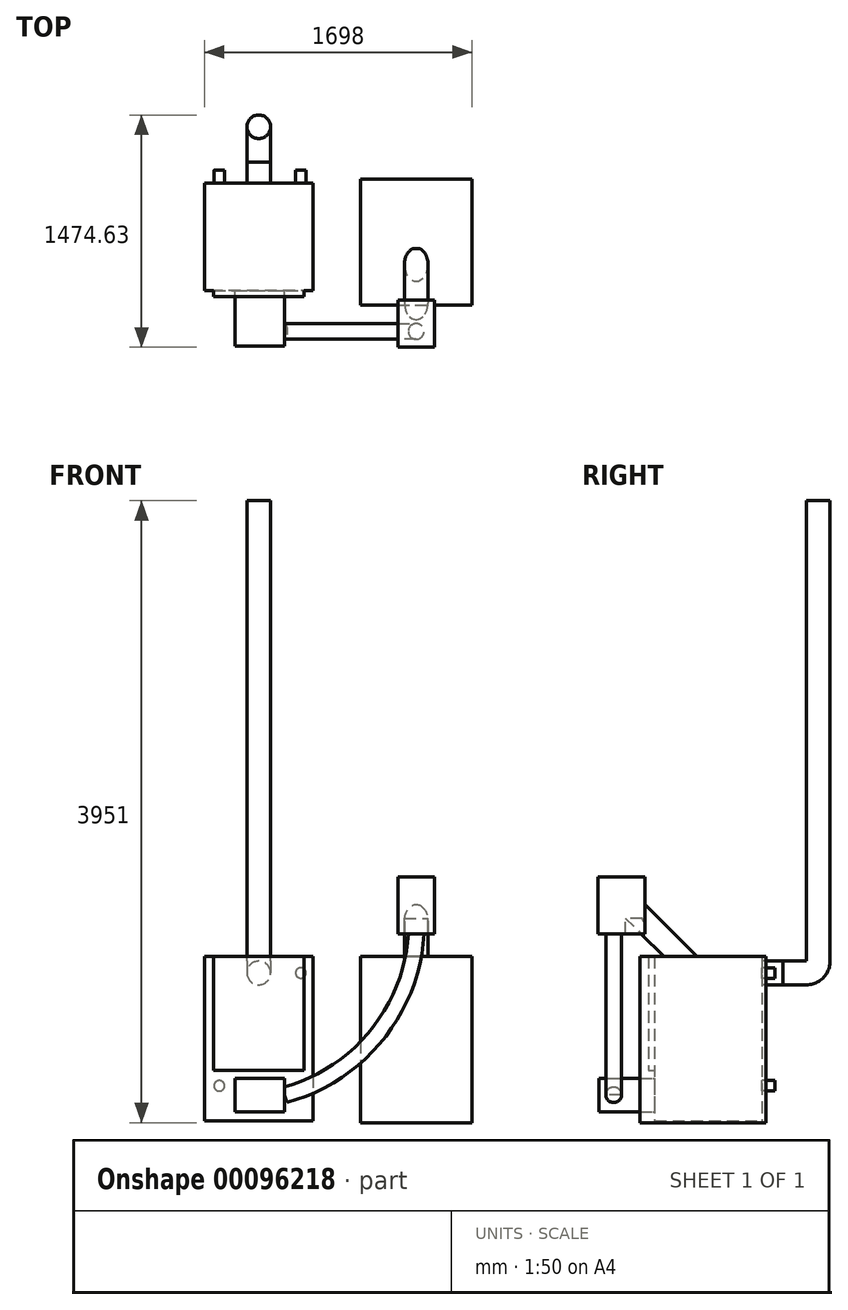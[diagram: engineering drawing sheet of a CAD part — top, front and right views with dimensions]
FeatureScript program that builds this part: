
annotation { "Feature Type Name" : "Feature", "Feature Type Description" : "" }
export const myFeature = defineFeature(function(context is Context, id is Id, definition is map)
    precondition{}
    {
        {
            var Q0;
            Q0=qCreatedBy(makeId("Front.planeOp"),FACE);
            var sketch = newSketch(context, id + "F0", { "sketchPlane" : qUnion([Q0])});
            skLineSegment(sketch, "E0.bottom", {"start": v(344, 522.5) * mm, "end": v(-344, 522.5) * mm});
            skLineSegment(sketch, "E0.top", {"start": v(344, -522.5) * mm, "end": v(-344, -522.5) * mm});
            skLineSegment(sketch, "E0.left", {"start": v(344, 522.5) * mm, "end": v(344, -522.5) * mm});
            skLineSegment(sketch, "E0.right", {"start": v(-344, 522.5) * mm, "end": v(-344, -522.5) * mm});
            skPoint(sketch, "E0.middle", {"position": v(0, 0) * mm});
            skSolve(sketch);
        }
        {
            var Q0;
            Q0 = qSketchRegion(id + "F0", true);
            extrude(context, id + "F1", {"entities" : qUnion([Q0]), "endBound" : BoundingType.SYMMETRIC, "depth" : 682 * mm});
        }
        {
            var Q0;
            Q0=makeQuery(id+"F1.opExtrude","CAP_FACE",FACE,{"disambiguationData":[OSD([sQuery(id+"F0.wireOp",EDGE,"E0.bottom"),sQuery(id+"F0.wireOp",EDGE,"E0.top"),sQuery(id+"F0.wireOp",EDGE,"E0.left"),sQuery(id+"F0.wireOp",EDGE,"E0.right")])],"isStart":false});
            var sketch = newSketch(context, id + "F2", { "sketchPlane" : qUnion([Q0])});
            skLineSegment(sketch, "E1.bottom", {"start": v(-287, 522.5) * mm, "end": v(287, 522.5) * mm});
            skLineSegment(sketch, "E1.top", {"start": v(-287, -200.5) * mm, "end": v(287, -200.5) * mm});
            skLineSegment(sketch, "E1.left", {"start": v(-287, 522.5) * mm, "end": v(-287, -200.5) * mm});
            skLineSegment(sketch, "E1.right", {"start": v(287, 522.5) * mm, "end": v(287, -200.5) * mm});
            skPoint(sketch, "E2", {"position": v(0, 522.5) * mm});
            skSolve(sketch);
        }
        {
            var Q0;
            Q0 = qSketchRegion(id + "F2", true);
            extrude(context, id + "F3", {"entities" : qUnion([Q0]), "operationType" : NewBodyOperationType.ADD, "depth" : 38.7 * mm});
        }
        {
            var Q0;
            Q0=makeQuery(id+"F1.opExtrude","CAP_FACE",FACE,{"disambiguationData":[OSD([sQuery(id+"F0.wireOp",EDGE,"E0.bottom"),sQuery(id+"F0.wireOp",EDGE,"E0.top"),sQuery(id+"F0.wireOp",EDGE,"E0.left"),sQuery(id+"F0.wireOp",EDGE,"E0.right")])],"isStart":false});
            var sketch = newSketch(context, id + "F4", { "sketchPlane" : qUnion([Q0])});
            skLineSegment(sketch, "E3.left", {"start": v(-151, -250.5) * mm, "end": v(-151, -463.5) * mm});
            skLineSegment(sketch, "E3.right", {"start": v(164, -250.5) * mm, "end": v(164, -463.5) * mm});
            skLineSegment(sketch, "E4", {"start": v(-151, -250.5) * mm, "end": v(164, -250.5) * mm});
            skLineSegment(sketch, "E5", {"start": v(164, -463.5) * mm, "end": v(-151, -463.5) * mm});
            skSolve(sketch);
        }
        {
            var Q0;
            Q0 = qSketchRegion(id + "F4", true);
            extrude(context, id + "F5", {"entities" : qUnion([Q0]), "operationType" : NewBodyOperationType.REMOVE, "oppositeDirection" : true, "depth" : 25 * mm});
        }
        {
            var Q0;
            Q0=makeQuery(id+"F1.opExtrude","CAP_FACE",FACE,{"disambiguationData":[OSD([sQuery(id+"F0.wireOp",EDGE,"E0.bottom"),sQuery(id+"F0.wireOp",EDGE,"E0.top"),sQuery(id+"F0.wireOp",EDGE,"E0.left"),sQuery(id+"F0.wireOp",EDGE,"E0.right")])],"isStart":true});
            var sketch = newSketch(context, id + "F6", { "sketchPlane" : qUnion([Q0])});
            skCircle(sketch, "E6", {"center": v(0, 418.5) * mm, "radius": 75 * mm});
            skSolve(sketch);
        }
        {
            var Q0;
            Q0 = qSketchRegion(id + "F6", true);
            extrude(context, id + "F7", {"entities" : qUnion([Q0]), "operationType" : NewBodyOperationType.ADD, "depth" : 132 * mm});
        }
        {
            var Q0;
            Q0=makeQuery(id+"F1.opExtrude","CAP_FACE",FACE,{"disambiguationData":[OSD([sQuery(id+"F0.wireOp",EDGE,"E0.bottom"),sQuery(id+"F0.wireOp",EDGE,"E0.top"),sQuery(id+"F0.wireOp",EDGE,"E0.left"),sQuery(id+"F0.wireOp",EDGE,"E0.right")])],"isStart":true});
            var sketch = newSketch(context, id + "F8", { "sketchPlane" : qUnion([Q0])});
            skCircle(sketch, "E7", {"center": v(250.65, -298.5) * mm, "radius": 33.5 * mm});
            skCircle(sketch, "E8", {"center": v(-267.35, 418.5) * mm, "radius": 33.5 * mm});
            skSolve(sketch);
        }
        {
            var Q0;
            Q0 = qSketchRegion(id + "F8", true);
            extrude(context, id + "F9", {"entities" : qUnion([Q0]), "operationType" : NewBodyOperationType.ADD, "depth" : 81 * mm});
        }
        {
            var Q0;
            Q0=makeQuery(id+"F7.opExtrude","CAP_FACE",FACE,{"disambiguationData":[OSD([sQuery(id+"F6.wireOp",EDGE,"E6")])],"isStart":false});
            var sketch = newSketch(context, id + "F10", { "sketchPlane" : qUnion([Q0])});
            skLineSegment(sketch, "E9", {"start": v(0, 418.5) * mm, "end": v(0, 338.5) * mm});
            skSolve(sketch);
        }
        {
            var Q0;
            Q0=sQuery(id+"F10.wireOp",EDGE,"E9");
            cPlane(context, id + "F11", {"entities" : qUnion([Q0]), "cplaneType" : CPlaneType.LINE_ANGLE, "offset" : 25 * mm, "angle" : 0 * degree, "width" : 150 * mm, "height" : 150 * mm});
        }
        {
            var Q0;
            Q0=qCreatedBy(id+"F11.planeOp",FACE);
            var sketch = newSketch(context, id + "F12", { "sketchPlane" : qUnion([Q0])});
            skLineSegment(sketch, "E10.0", {"start": v(-473, 343.5) * mm, "end": v(-473, 493.5) * mm});
            skLineSegment(sketch, "E11", {"start": v(-473, 418.5) * mm, "end": v(-623, 418.5) * mm});
            skLineSegment(sketch, "E12", {"start": v(-698, 493.5) * mm, "end": v(-698, 3418.5) * mm});
            skPoint(sketch, "E13.visualSharp", {"position": v(-698, 418.5) * mm});
            skArc(sketch, "E13.filletArc", {"start": v(-698, 493.5) * mm, "mid": v(-676.03, 440.47) * mm, "end": v(-623, 418.5) * mm});
            skLineSegment(sketch, "E14.0", {"start": v(-623, 493.5) * mm, "end": v(-623, 3418.5) * mm});
            skLineSegment(sketch, "E14.1", {"start": v(-473, 493.5) * mm, "end": v(-623, 493.5) * mm});
            skLineSegment(sketch, "E15.0", {"start": v(-773, 493.5) * mm, "end": v(-773, 3418.5) * mm});
            skArc(sketch, "E15.1", {"start": v(-773, 493.5) * mm, "mid": v(-729.07, 387.43) * mm, "end": v(-623, 343.5) * mm});
            skLineSegment(sketch, "E15.2", {"start": v(-473, 343.5) * mm, "end": v(-623, 343.5) * mm});
            skLineSegment(sketch, "E16", {"start": v(-623, 3418.5) * mm, "end": v(-773, 3418.5) * mm});
            skSolve(sketch);
        }
        {
            var Q0;
            Q0=makeQuery(id+"F10.imprint","IMPRINT",FACE,{"disambiguationData":[TD([[makeQuery(id+"F10.imprint","IMPRINT",EDGE,{"derivedFrom":makeQuery(id+"F7.opExtrude","CAP_EDGE",EDGE,{"disambiguationData":[OSD([sQuery(id+"F6.wireOp",EDGE,"E6")])],"isStart":false})}),1.0]])]});
            var Q1;
            Q1=sQuery(id+"F12.wireOp",EDGE,"E11");
            var Q2;
            Q2=sQuery(id+"F12.wireOp",EDGE,"E13.filletArc");
            var Q3;
            Q3=sQuery(id+"F12.wireOp",EDGE,"E12");
            sweep(context, id + "F13", {"profiles" : qUnion([Q0]), "path" : qUnion([Q1, Q2, Q3])});
        }
        {
            var Q0;
            Q0=makeQuery(id+"F1.opExtrude","CAP_FACE",FACE,{"disambiguationData":[OSD([sQuery(id+"F0.wireOp",EDGE,"E0.bottom"),sQuery(id+"F0.wireOp",EDGE,"E0.top"),sQuery(id+"F0.wireOp",EDGE,"E0.left"),sQuery(id+"F0.wireOp",EDGE,"E0.right")])],"isStart":true});
            cPlane(context, id + "F14", {"entities" : qUnion([Q0]), "cplaneType" : CPlaneType.OFFSET, "offset" : 25 * mm, "width" : 150 * mm, "height" : 150 * mm});
        }
        {
            var Q0;
            Q0=qCreatedBy(id+"F14.planeOp",FACE);
            var sketch = newSketch(context, id + "F15", { "sketchPlane" : qUnion([Q0])});
            skLineSegment(sketch, "E17.1.0.0", {"start": v(-646, 522.5) * mm, "end": v(-1354, 522.5) * mm});
            skLineSegment(sketch, "E17.1.0.1", {"start": v(-646, 522.5) * mm, "end": v(-646, -532.5) * mm});
            skLineSegment(sketch, "E17.1.0.2", {"start": v(-1354, 522.5) * mm, "end": v(-1354, -532.5) * mm});
            skLineSegment(sketch, "E18", {"start": v(-646, -532.5) * mm, "end": v(-1354, -532.5) * mm});
            skSolve(sketch);
        }
        {
            var Q0;
            Q0 = qSketchRegion(id + "F15", true);
            extrude(context, id + "F16", {"entities" : qUnion([Q0]), "oppositeDirection" : true, "depth" : 800 * mm});
        }
        {
            var Q0;
            Q0=makeQuery(id+"F16.opExtrude","SWEPT_FACE",FACE,{"disambiguationData":[OSD([sQuery(id+"F15.wireOp",EDGE,"E17.1.0.0")])]});
            var sketch = newSketch(context, id + "F17", { "sketchPlane" : qUnion([Q0])});
            skLineSegment(sketch, "E19.0", {"start": v(646, -290) * mm, "end": v(1354, -290) * mm});
            skSolve(sketch);
        }
        {
            var Q0;
            Q0=sQuery(id+"F17.wireOp",EDGE,"E19.0");
            cPlane(context, id + "F18", {"entities" : qUnion([Q0]), "cplaneType" : CPlaneType.LINE_ANGLE, "offset" : 25 * mm, "angle" : 45 * degree, "oppositeDirection" : true, "width" : 150 * mm, "height" : 150 * mm});
        }
        {
            var Q0;
            Q0=qCreatedBy(id+"F18.planeOp",FACE);
            cPlane(context, id + "F19", {"entities" : qUnion([Q0]), "cplaneType" : CPlaneType.OFFSET, "offset" : 150 * mm, "width" : 150 * mm, "height" : 150 * mm});
        }
        {
            var Q0;
            Q0=qCreatedBy(id+"F19.planeOp",FACE);
            var sketch = newSketch(context, id + "F20", { "sketchPlane" : qUnion([Q0])});
            skCircle(sketch, "E20", {"center": v(-1000, 244.4) * mm, "radius": 75 * mm});
            skSolve(sketch);
        }
        {
            var Q0;
            Q0 = qSketchRegion(id + "F20", true);
            var Q1;
            Q1=sQuery(id+"F20.wireOp",EDGE,"E20");
            extrude(context, id + "F21", {"entities" : qUnion([Q0]), "operationType" : NewBodyOperationType.ADD, "surfaceEntities" : qUnion([Q1]), "oppositeDirection" : true, "depth" : 600 * mm});
        }
        {
            var Q0;
            Q0=makeQuery(id+"F21.opExtrude","CAP_FACE",FACE,{"disambiguationData":[OSD([sQuery(id+"F20.wireOp",EDGE,"E20")])],"isStart":false});
            var sketch = newSketch(context, id + "F22", { "sketchPlane" : qUnion([Q0])});
            skLineSegment(sketch, "E21", {"start": v(1000, 244.4) * mm, "end": v(1084.1, 244.4) * mm});
            skSolve(sketch);
        }
        {
            var Q0;
            Q0=sQuery(id+"F22.wireOp",EDGE,"E21");
            cPlane(context, id + "F23", {"entities" : qUnion([Q0]), "cplaneType" : CPlaneType.LINE_ANGLE, "offset" : 25 * mm, "angle" : 0 * degree, "width" : 150 * mm, "height" : 150 * mm});
        }
        {
            var Q0;
            Q0=qCreatedBy(id+"F23.planeOp",FACE);
            var sketch = newSketch(context, id + "F24", { "sketchPlane" : qUnion([Q0])});
            skLineSegment(sketch, "E22.0", {"start": v(-1000, 897.27) * mm, "end": v(-1084.1, 897.27) * mm});
            skLineSegment(sketch, "E23.bottom", {"start": v(-1117.19, 1028.23) * mm, "end": v(-882.81, 1028.23) * mm});
            skLineSegment(sketch, "E23.top", {"start": v(-1117.19, 766.3) * mm, "end": v(-882.81, 766.3) * mm});
            skLineSegment(sketch, "E23.left", {"start": v(-1117.19, 1028.23) * mm, "end": v(-1117.19, 766.3) * mm});
            skLineSegment(sketch, "E23.right", {"start": v(-882.81, 1028.23) * mm, "end": v(-882.81, 766.3) * mm});
            skPoint(sketch, "E23.middle", {"position": v(-1000, 897.27) * mm});
            skSolve(sketch);
        }
        {
            var Q0;
            Q0 = qSketchRegion(id + "F24", true);
            extrude(context, id + "F25", {"entities" : qUnion([Q0]), "operationType" : NewBodyOperationType.ADD, "endBound" : BoundingType.SYMMETRIC, "depth" : 300 * mm});
        }
        {
            var Q0;
            Q0=makeQuery(id+"F25.opExtrude","SWEPT_FACE",FACE,{"disambiguationData":[OSD([sQuery(id+"F24.wireOp",EDGE,"E23.top")])]});
            extrude(context, id + "F26", {"entities" : qUnion([Q0]), "operationType" : NewBodyOperationType.ADD, "depth" : 100 * mm});
        }
        {
            var Q0;
            Q0=makeQuery(id+"F26.opExtrude","CAP_FACE",FACE,{"disambiguationData":[OSD([sQuery(id+"F24.wireOp",EDGE,"E23.top")])],"isStart":false});
            var sketch = newSketch(context, id + "F27", { "sketchPlane" : qUnion([Q0])});
            skLineSegment(sketch, "E24.0", {"start": v(1117.19, 601.63) * mm, "end": v(882.81, 601.63) * mm});
            skCircle(sketch, "E25", {"center": v(1000, 601.63) * mm, "radius": 50 * mm});
            skSolve(sketch);
        }
        {
            var Q0;
            Q0=sQuery(id+"F27.wireOp",EDGE,"E24.0");
            cPlane(context, id + "F28", {"entities" : qUnion([Q0]), "cplaneType" : CPlaneType.LINE_ANGLE, "offset" : 25 * mm, "angle" : 0 * degree, "width" : 150 * mm, "height" : 150 * mm});
        }
        {
            var Q0;
            Q0=qCreatedBy(id+"F28.planeOp",FACE);
            var sketch = newSketch(context, id + "F29", { "sketchPlane" : qUnion([Q0])});
            skLineSegment(sketch, "E26.0", {"start": v(1050, 666.3) * mm, "end": v(950, 666.3) * mm});
            skLineSegment(sketch, "E27.0", {"start": v(164, -250.5) * mm, "end": v(164, -463.5) * mm});
            skArc(sketch, "E28", {"start": v(164, -357) * mm, "mid": v(746.38, 20.36) * mm, "end": v(1000, 666.3) * mm});
            skSolve(sketch);
        }
        {
            var Q0;
            Q0=makeQuery(id+"F26.opExtrude","CAP_FACE",FACE,{"disambiguationData":[OSD([sQuery(id+"F24.wireOp",EDGE,"E23.top")])],"isStart":false});
            var sketch = newSketch(context, id + "F30", { "sketchPlane" : qUnion([Q0])});
            skCircle(sketch, "E29.0", {"center": v(1000, 601.63) * mm, "radius": 50 * mm});
            skSolve(sketch);
        }
        {
            var Q0;
            Q0=makeQuery(id+"F30.imprint","IMPRINT",FACE,{"disambiguationData":[TD([[makeQuery(id+"F30.imprint","IMPRINT",EDGE,{"derivedFrom":sQuery(id+"F30.wireOp",EDGE,"E29.0")}),1.0]])]});
            var Q1;
            Q1=sQuery(id+"F29.wireOp",EDGE,"E28");
            sweep(context, id + "F31", {"profiles" : qUnion([Q0]), "path" : qUnion([Q1])});
        }
        {
            var Q0;
            Q0=makeQuery(id+"F5.boolean.opBoolean","COPY",FACE,{"derivedFrom":makeQuery(id+"F5.opExtrude","CAP_FACE",FACE,{"disambiguationData":[OSD([sQuery(id+"F4.wireOp",EDGE,"E3.left"),sQuery(id+"F4.wireOp",EDGE,"E3.right"),sQuery(id+"F4.wireOp",EDGE,"E4"),sQuery(id+"F4.wireOp",EDGE,"E5")])],"isStart":false})});
            extrude(context, id + "F32", {"entities" : qUnion([Q0]), "operationType" : NewBodyOperationType.ADD, "depth" : 380 * mm});
        }
    });
